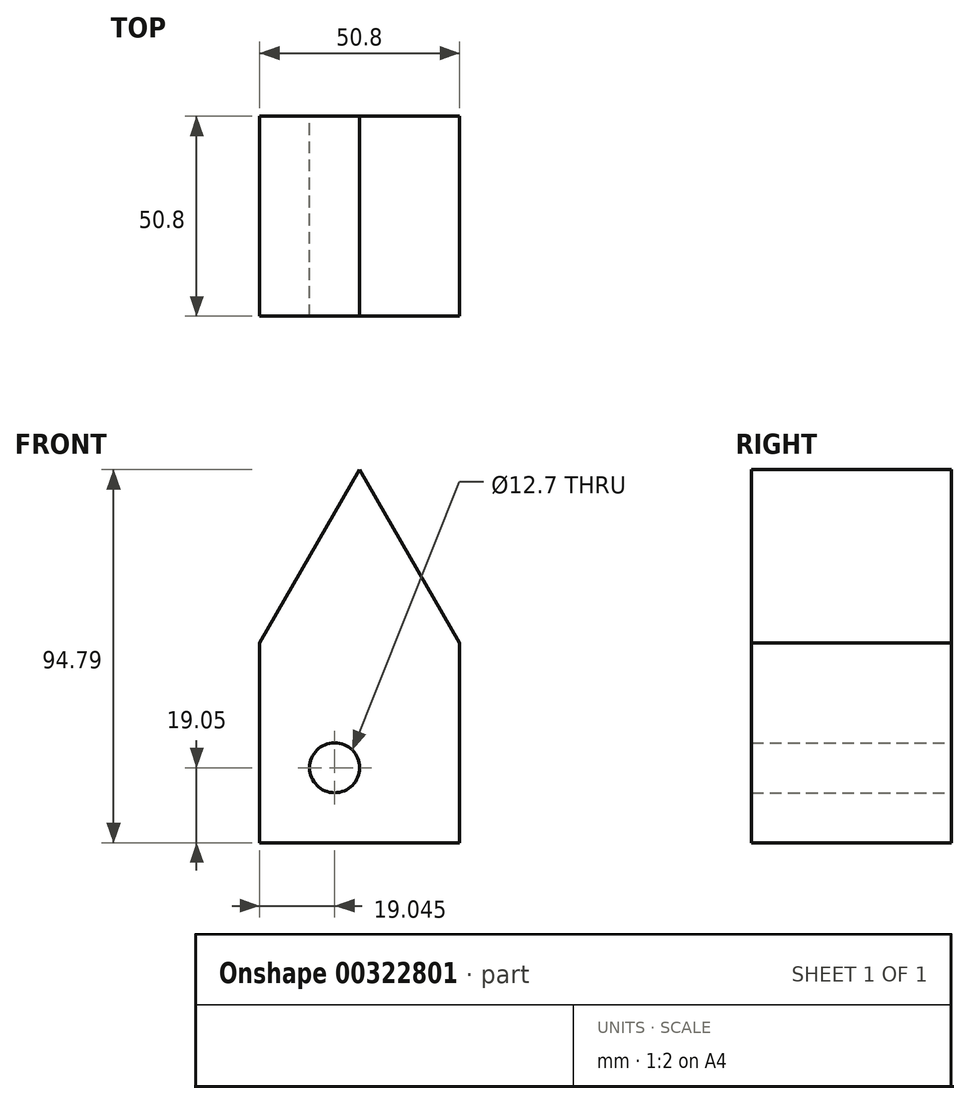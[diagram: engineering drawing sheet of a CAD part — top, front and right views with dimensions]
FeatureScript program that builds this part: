
annotation { "Feature Type Name" : "Feature", "Feature Type Description" : "" }
export const myFeature = defineFeature(function(context is Context, id is Id, definition is map)
    precondition{}
    {
        {
            var Q0;
            Q0=qCreatedBy(makeId("Front.planeOp"),FACE);
            var sketch = newSketch(context, id + "F0", { "sketchPlane" : qUnion([Q0])});
            skLineSegment(sketch, "E0.top", {"start": v(-20.91, -30.63) * mm, "end": v(29.89, -30.63) * mm});
            skLineSegment(sketch, "E0.left", {"start": v(-20.91, 20.17) * mm, "end": v(-20.91, -30.63) * mm});
            skLineSegment(sketch, "E0.right", {"start": v(29.89, 20.17) * mm, "end": v(29.89, -30.63) * mm});
            skLineSegment(sketch, "E1", {"start": v(-20.91, 20.17) * mm, "end": v(4.49, 64.16) * mm});
            skLineSegment(sketch, "E2", {"start": v(4.49, 64.16) * mm, "end": v(29.89, 20.17) * mm});
            skCircle(sketch, "E3", {"center": v(-1.86, -11.58) * mm, "radius": 6.35 * mm});
            skSolve(sketch);
        }
        {
            var Q0;
            Q0=makeQuery(id+"F0.imprint","IMPRINT",FACE,{"disambiguationData":[TD([[makeQuery(id+"F0.imprint","IMPRINT",EDGE,{"derivedFrom":sQuery(id+"F0.wireOp",EDGE,"E0.top")}),1.0]])]});
            extrude(context, id + "F1", {"entities" : qUnion([Q0]), "depth" : 50.8 * mm});
        }
    });
